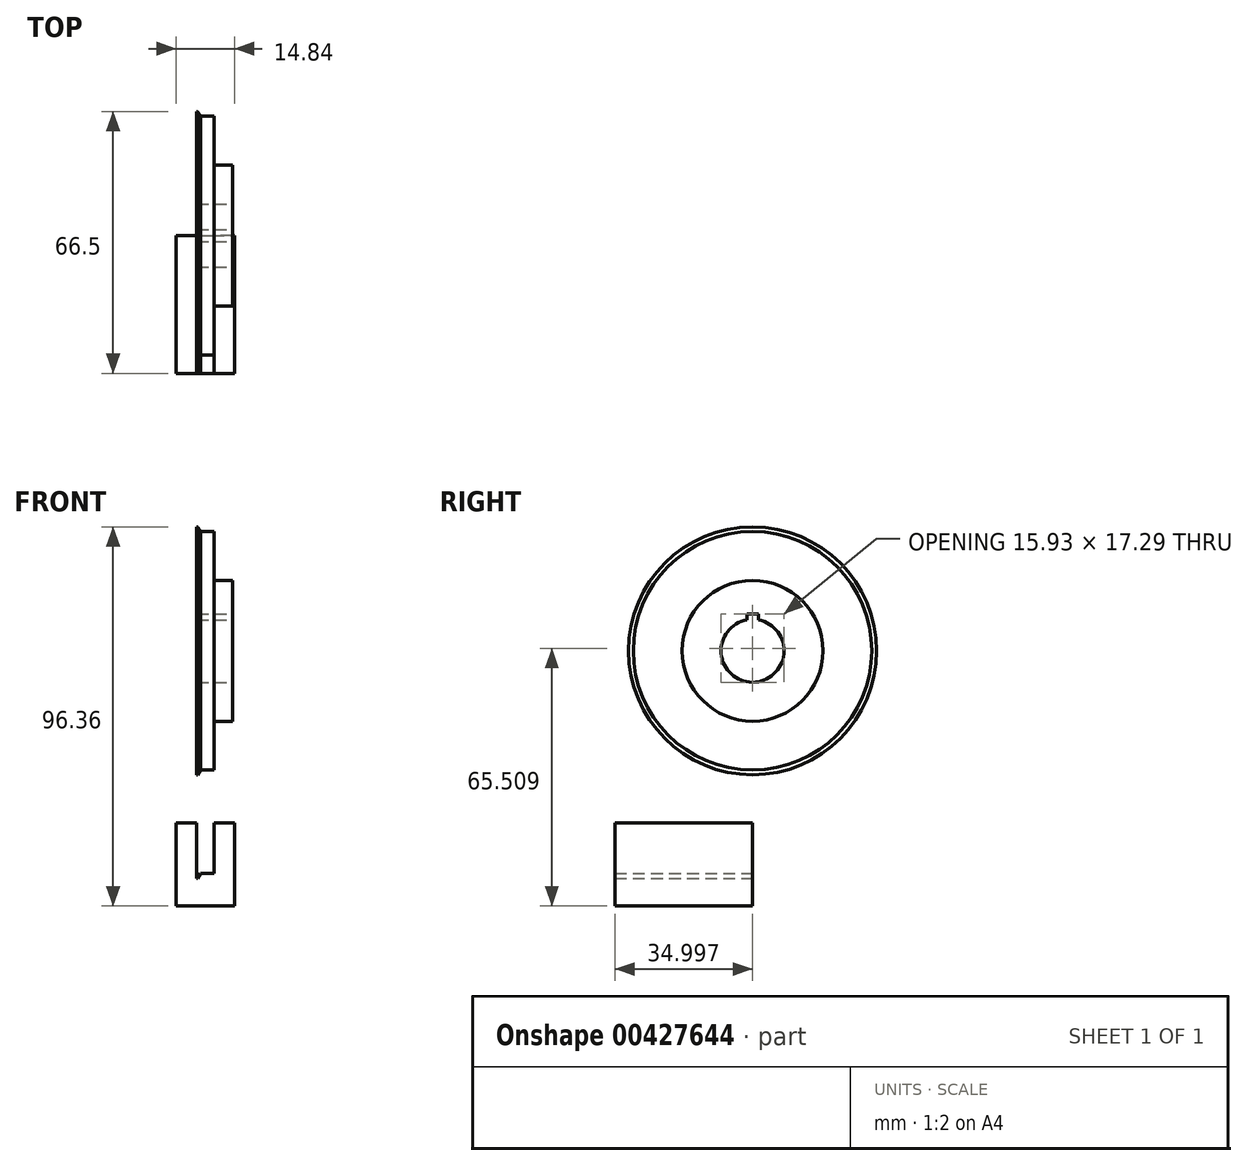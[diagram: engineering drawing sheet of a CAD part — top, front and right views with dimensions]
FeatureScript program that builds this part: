
annotation { "Feature Type Name" : "Feature", "Feature Type Description" : "" }
export const myFeature = defineFeature(function(context is Context, id is Id, definition is map)
    precondition{}
    {
        {
            var Q0;
            Q0=qCreatedBy(makeId("Front.planeOp"),FACE);
            var sketch = newSketch(context, id + "F0", { "sketchPlane" : qUnion([Q0])});
            skLineSegment(sketch, "E0", {"start": v(0, -1.75) * mm, "end": v(0.3, -1.75) * mm});
            skLineSegment(sketch, "E1", {"start": v(0.3, -1.75) * mm, "end": v(1, -0.55) * mm});
            skLineSegment(sketch, "E2", {"start": v(1, -0.55) * mm, "end": v(4.5, -0.55) * mm});
            skLineSegment(sketch, "E3", {"start": v(0, -1.75) * mm, "end": v(0, 29.75) * mm});
            skLineSegment(sketch, "E4", {"start": v(4.5, -0.55) * mm, "end": v(4.5, 11.86) * mm});
            skLineSegment(sketch, "E5", {"start": v(4.5, 11.86) * mm, "end": v(9.14, 11.86) * mm});
            skLineSegment(sketch, "E6", {"start": v(9.14, 11.86) * mm, "end": v(9.14, 29.75) * mm});
            skLineSegment(sketch, "E7", {"start": v(0, 29.75) * mm, "end": v(9.14, 29.75) * mm});
            skSolve(sketch);
        }
        {
            var Q0;
            Q0=makeQuery(id+"F0.imprint","IMPRINT",FACE,{"disambiguationData":[TD([[makeQuery(id+"F0.imprint","IMPRINT",EDGE,{"derivedFrom":sQuery(id+"F0.wireOp",EDGE,"E0")}),1.0]])]});
            var Q1;
            Q1=sQuery(id+"F0.wireOp",EDGE,"E7");
            revolve(context, id + "F1", {"entities" : qUnion([Q0]), "axis" : qUnion([Q1]), "revolveType" : RevolveType.FULL});
        }
        {
            var Q0;
            Q0=qCreatedBy(makeId("Front.planeOp"),FACE);
            var sketch = newSketch(context, id + "F2", { "sketchPlane" : qUnion([Q0])});
            skLineSegment(sketch, "E8", {"start": v(1, -26.83) * mm, "end": v(4.5, -26.83) * mm});
            skLineSegment(sketch, "E9", {"start": v(4.5, -26.83) * mm, "end": v(4.5, -14.03) * mm});
            skLineSegment(sketch, "E10", {"start": v(0, -28.03) * mm, "end": v(0, -14.03) * mm});
            skLineSegment(sketch, "E11", {"start": v(0, -28.03) * mm, "end": v(0.3, -28.03) * mm});
            skLineSegment(sketch, "E12", {"start": v(0.3, -28.03) * mm, "end": v(1, -26.83) * mm});
            skLineSegment(sketch, "E13", {"start": v(0, -14.03) * mm, "end": v(-5.18, -14.03) * mm});
            skLineSegment(sketch, "E14", {"start": v(-5.18, -14.03) * mm, "end": v(-5.18, -35.11) * mm});
            skLineSegment(sketch, "E15", {"start": v(-5.18, -35.11) * mm, "end": v(9.66, -35.11) * mm});
            skLineSegment(sketch, "E16", {"start": v(9.66, -35.11) * mm, "end": v(9.66, -14.03) * mm});
            skLineSegment(sketch, "E17", {"start": v(9.66, -14.03) * mm, "end": v(4.5, -14.03) * mm});
            skSolve(sketch);
        }
        {
            var Q0;
            Q0=makeQuery(id+"F2.imprint","IMPRINT",FACE,{"disambiguationData":[TD([[makeQuery(id+"F2.imprint","IMPRINT",EDGE,{"derivedFrom":sQuery(id+"F2.wireOp",EDGE,"E8")}),-1.0]])]});
            extrude(context, id + "F3", {"entities" : qUnion([Q0]), "depth" : 35 * mm});
        }
        {
            var Q0;
            Q0=makeQuery(id+"F1.opRevolve","SWEPT_FACE",FACE,{"disambiguationData":[OSD([sQuery(id+"F0.wireOp",EDGE,"E6")])]});
            var sketch = newSketch(context, id + "F4", { "sketchPlane" : qUnion([Q0])});
            skCircle(sketch, "E18", {"center": v(0, 29.75) * mm, "radius": 8 * mm});
            skSolve(sketch);
        }
        {
            var Q0;
            Q0=makeQuery(id+"F4.imprint","IMPRINT",FACE,{"disambiguationData":[TD([[makeQuery(id+"F4.imprint","IMPRINT",EDGE,{"derivedFrom":sQuery(id+"F4.wireOp",EDGE,"E18")}),1.0]])]});
            extrude(context, id + "F5", {"entities" : qUnion([Q0]), "operationType" : NewBodyOperationType.REMOVE, "oppositeDirection" : true, "depth" : 25 * mm});
        }
        {
            var Q0;
            Q0=makeQuery(id+"F1.opRevolve","SWEPT_FACE",FACE,{"disambiguationData":[OSD([sQuery(id+"F0.wireOp",EDGE,"E6")])]});
            var sketch = newSketch(context, id + "F6", { "sketchPlane" : qUnion([Q0])});
            skLineSegment(sketch, "E19.top", {"start": v(-1.47, 39.05) * mm, "end": v(1.54, 39.05) * mm});
            skLineSegment(sketch, "E19.left", {"start": v(-1.47, 37.62) * mm, "end": v(-1.47, 39.05) * mm});
            skLineSegment(sketch, "E19.right", {"start": v(1.54, 37.6) * mm, "end": v(1.54, 39.05) * mm});
            skArc(sketch, "E20", {"start": v(1.54, 37.6) * mm, "mid": v(0.04, 37.75) * mm, "end": v(-1.47, 37.62) * mm});
            skSolve(sketch);
        }
        {
            var Q0;
            Q0=makeQuery(id+"F6.imprint","IMPRINT",FACE,{"disambiguationData":[TD([[makeQuery(id+"F6.imprint","IMPRINT",EDGE,{"derivedFrom":sQuery(id+"F6.wireOp",EDGE,"E19.top")}),-1.0]])]});
            extrude(context, id + "F7", {"entities" : qUnion([Q0]), "operationType" : NewBodyOperationType.REMOVE, "oppositeDirection" : true, "depth" : 25 * mm});
        }
    });
